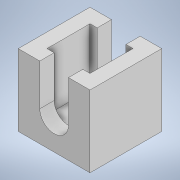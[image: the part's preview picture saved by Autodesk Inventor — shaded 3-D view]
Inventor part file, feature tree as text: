
AUTODESK INVENTOR PART (.ipt)
format: ipt  version: 2022 (Build 260153000, 153)  size: 111,104 bytes
history: native  units: in
note: dims shown in document units (in); Inventor stores cm internally (conversion verified against a paired STEP export)
features: extrude x2, sketch x2, shell x1
ambient origin geometry x8: Origin, YZ Plane, XZ Plane, XY Plane, X Axis, Y Axis, Z Axis, Center Point
bodies: Solid1 (feature_tree)
feature tree (5):
  extrude  "Extrusion1"  Depth=0.1969in
  shell  "Shell1"  Thickness=0.1969in
  extrude  "Extrusion3"  TaperAngle=0.0deg  [1 undecoded]
  sketch  "Sketch1"  dims[d0=0.1969in d1=0.1969in d2=0.1969in d3=0.0in]
  sketch  "Sketch3"  dims[d4=0.0394in d8=0.0in d9=0.0in]
note: 1 required parameter value undecoded (feature->parameter linkage not recoverable at this tier; creation-order binding heuristic only, values carry confidence <= 0.55)
